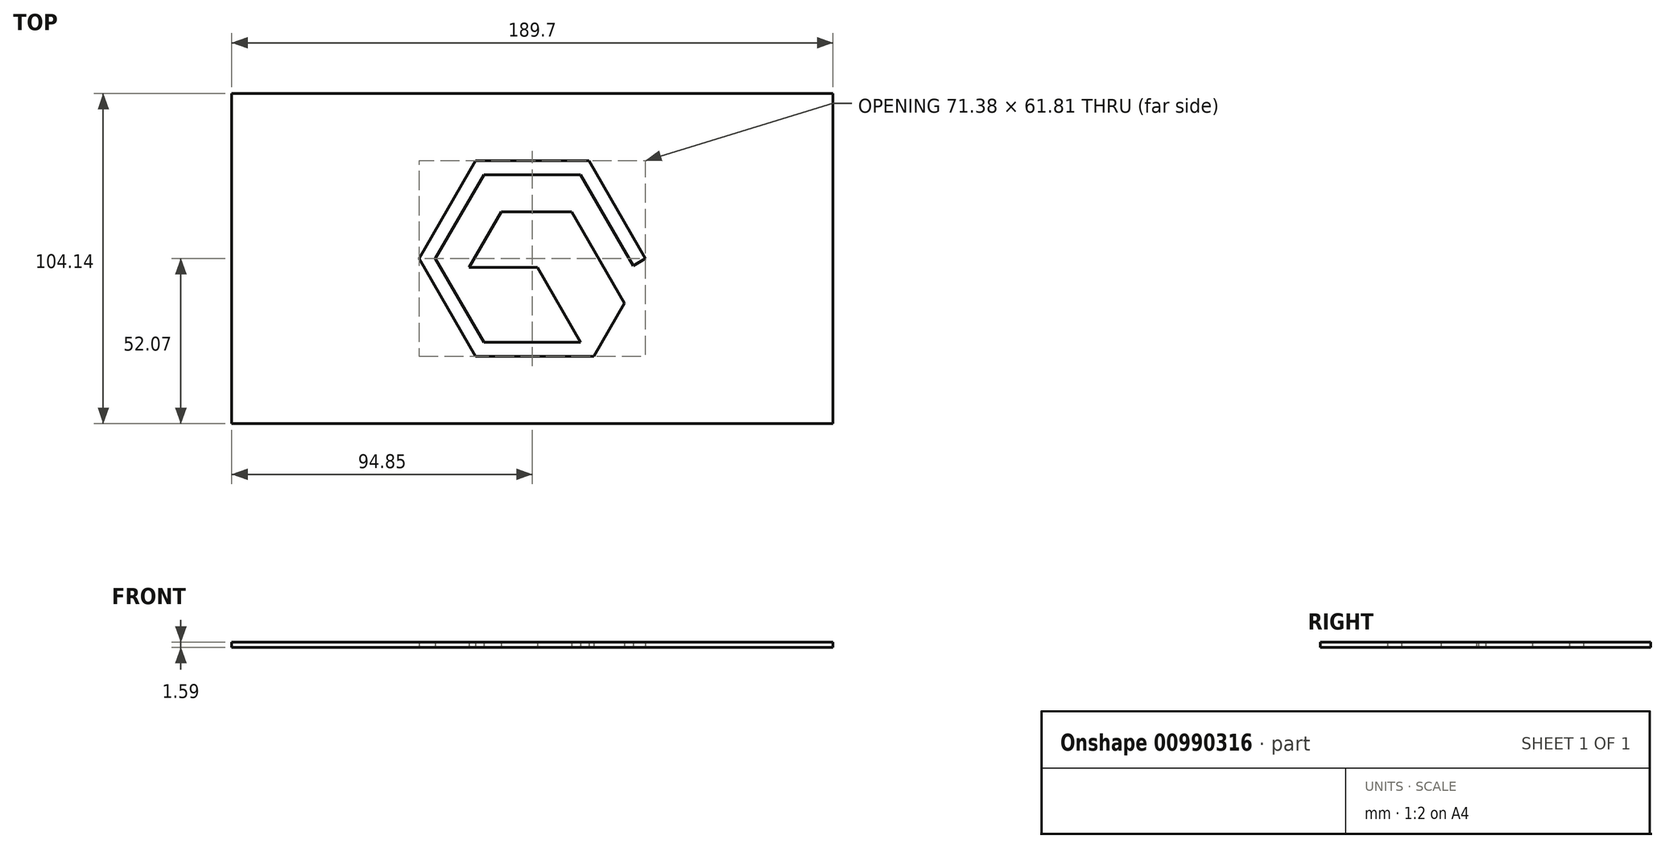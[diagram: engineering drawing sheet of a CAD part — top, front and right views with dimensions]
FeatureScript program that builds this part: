
annotation { "Feature Type Name" : "Feature", "Feature Type Description" : "" }
export const myFeature = defineFeature(function(context is Context, id is Id, definition is map)
    precondition{}
    {
        {
            var Q0;
            Q0=qCreatedBy(makeId("Top.planeOp"),FACE);
            var sketch = newSketch(context, id + "F0", { "sketchPlane" : qUnion([Q0])});
            skLineSegment(sketch, "E0", {"start": v(2.07, -30.9) * mm, "end": v(39.33, -30.9) * mm});
            skLineSegment(sketch, "E1", {"start": v(39.33, -30.9) * mm, "end": v(49.04, -14.09) * mm});
            skLineSegment(sketch, "E2", {"start": v(49.04, -14.09) * mm, "end": v(32.37, 14.79) * mm});
            skLineSegment(sketch, "E3", {"start": v(32.37, 14.79) * mm, "end": v(10.17, 14.79) * mm});
            skLineSegment(sketch, "E4", {"start": v(10.17, 14.79) * mm, "end": v(0, -2.82) * mm});
            skLineSegment(sketch, "E5", {"start": v(0, -2.82) * mm, "end": v(21.54, -2.82) * mm});
            skLineSegment(sketch, "E6", {"start": v(4.63, -26.46) * mm, "end": v(-10.65, 0) * mm});
            skLineSegment(sketch, "E7", {"start": v(-10.65, 0) * mm, "end": v(4.63, 26.46) * mm});
            skLineSegment(sketch, "E8", {"start": v(4.63, 26.46) * mm, "end": v(35.19, 26.46) * mm});
            skLineSegment(sketch, "E9", {"start": v(35.19, 26.46) * mm, "end": v(51.75, -2.22) * mm});
            skLineSegment(sketch, "E10", {"start": v(51.75, -2.22) * mm, "end": v(55.6, 0) * mm});
            skLineSegment(sketch, "E11", {"start": v(55.6, 0) * mm, "end": v(37.75, 30.9) * mm});
            skLineSegment(sketch, "E12", {"start": v(37.75, 30.9) * mm, "end": v(2.07, 30.9) * mm});
            skLineSegment(sketch, "E13", {"start": v(2.07, 30.9) * mm, "end": v(-15.78, 0) * mm});
            skLineSegment(sketch, "E14", {"start": v(-15.78, 0) * mm, "end": v(2.07, -30.9) * mm});
            skLineSegment(sketch, "E15", {"start": v(4.63, -26.46) * mm, "end": v(35.19, -26.46) * mm});
            skLineSegment(sketch, "E16", {"start": v(21.54, -2.82) * mm, "end": v(35.19, -26.46) * mm});
            skLineSegment(sketch, "E17.bottom", {"start": v(114.76, -52.07) * mm, "end": v(-74.94, -52.07) * mm});
            skLineSegment(sketch, "E17.top", {"start": v(114.76, 52.07) * mm, "end": v(-74.94, 52.07) * mm});
            skLineSegment(sketch, "E17.left", {"start": v(114.76, -52.07) * mm, "end": v(114.76, 52.07) * mm});
            skLineSegment(sketch, "E17.right", {"start": v(-74.94, -52.07) * mm, "end": v(-74.94, 52.07) * mm});
            skPoint(sketch, "E17.middle", {"position": v(19.91, 0) * mm});
            skLineSegment(sketch, "E18", {"start": v(19.91, 30.9) * mm, "end": v(19.91, -30.9) * mm, "construction": true});
            skPoint(sketch, "E18.endSnap0", {"position": v(19.91, 26.46) * mm});
            skLineSegment(sketch, "E19", {"start": v(-15.78, 0) * mm, "end": v(55.6, 0) * mm, "construction": true});
            skSolve(sketch);
        }
        {
            var Q0;
            Q0=makeQuery(id+"F0.imprint","IMPRINT",FACE,{"disambiguationData":[TD([[makeQuery(id+"F0.imprint","IMPRINT",EDGE,{"derivedFrom":sQuery(id+"F0.wireOp",EDGE,"E0")}),-1.0]])]});
            extrude(context, id + "F1", {"entities" : qUnion([Q0]), "depth" : 1.59 * mm, "offsetDistance" : 25.4 * mm});
        }
    });
